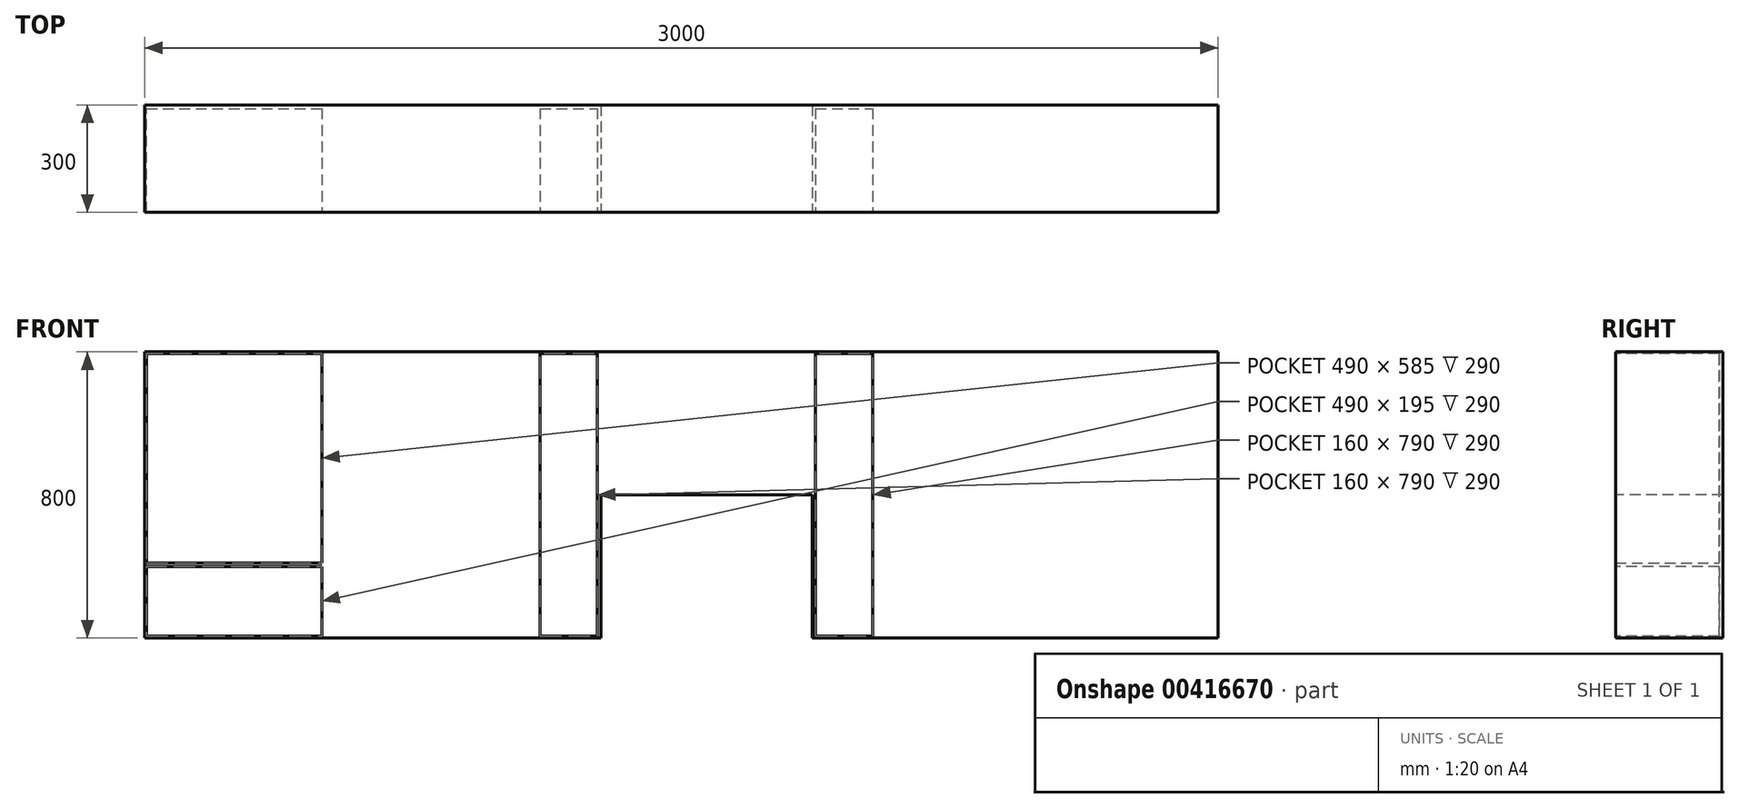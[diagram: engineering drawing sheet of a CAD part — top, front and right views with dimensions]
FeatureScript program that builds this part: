
annotation { "Feature Type Name" : "Feature", "Feature Type Description" : "" }
export const myFeature = defineFeature(function(context is Context, id is Id, definition is map)
    precondition{}
    {
        {
            var Q0;
            Q0=qCreatedBy(makeId("Front.planeOp"),FACE);
            var sketch = newSketch(context, id + "F0", { "sketchPlane" : qUnion([Q0])});
            skLineSegment(sketch, "E0.bottom", {"start": v(0, 0) * mm, "end": v(3000, 0) * mm});
            skLineSegment(sketch, "E0.top", {"start": v(0, 800) * mm, "end": v(3000, 800) * mm});
            skLineSegment(sketch, "E0.left", {"start": v(0, 0) * mm, "end": v(0, 800) * mm});
            skLineSegment(sketch, "E0.right", {"start": v(3000, 0) * mm, "end": v(3000, 800) * mm});
            skSolve(sketch);
        }
        {
            var Q0;
            Q0 = qSketchRegion(id + "F0", true);
            extrude(context, id + "F1", {"entities" : qUnion([Q0]), "depth" : 300 * mm});
        }
        {
            var Q0;
            Q0=makeQuery(id+"F1.opExtrude","CAP_FACE",FACE,{"disambiguationData":[OSD([sQuery(id+"F0.wireOp",EDGE,"E0.bottom"),sQuery(id+"F0.wireOp",EDGE,"E0.top"),sQuery(id+"F0.wireOp",EDGE,"E0.left"),sQuery(id+"F0.wireOp",EDGE,"E0.right")])],"isStart":false});
            var sketch = newSketch(context, id + "F2", { "sketchPlane" : qUnion([Q0])});
            skLineSegment(sketch, "E1.bottom", {"start": v(0, 0) * mm, "end": v(500, 0) * mm});
            skLineSegment(sketch, "E1.top", {"start": v(0, 800) * mm, "end": v(500, 800) * mm});
            skLineSegment(sketch, "E1.left", {"start": v(0, 0) * mm, "end": v(0, 800) * mm});
            skLineSegment(sketch, "E1.right", {"start": v(500, 0) * mm, "end": v(500, 800) * mm});
            skLineSegment(sketch, "E2.0", {"start": v(5, 795) * mm, "end": v(495, 795) * mm});
            skLineSegment(sketch, "E2.1", {"start": v(5, 5) * mm, "end": v(5, 795) * mm});
            skLineSegment(sketch, "E2.2", {"start": v(5, 5) * mm, "end": v(495, 5) * mm});
            skLineSegment(sketch, "E2.3", {"start": v(495, 5) * mm, "end": v(495, 795) * mm});
            skSolve(sketch);
        }
        {
            var Q0;
            Q0=makeQuery(id+"F2.imprint","IMPRINT",FACE,{"disambiguationData":[TD([[makeQuery(id+"F2.imprint","IMPRINT",EDGE,{"derivedFrom":sQuery(id+"F2.wireOp",EDGE,"E2.0")}),-1.0]])]});
            extrude(context, id + "F3", {"entities" : qUnion([Q0]), "operationType" : NewBodyOperationType.REMOVE, "oppositeDirection" : true, "depth" : 290 * mm});
        }
        {
            var Q0;
            Q0=makeQuery(id+"F1.opExtrude","CAP_FACE",FACE,{"disambiguationData":[OSD([sQuery(id+"F0.wireOp",EDGE,"E0.bottom"),sQuery(id+"F0.wireOp",EDGE,"E0.top"),sQuery(id+"F0.wireOp",EDGE,"E0.left"),sQuery(id+"F0.wireOp",EDGE,"E0.right")])],"isStart":false});
            var sketch = newSketch(context, id + "F4", { "sketchPlane" : qUnion([Q0])});
            skLineSegment(sketch, "E3.bottom", {"start": v(1100, 800) * mm, "end": v(1270, 800) * mm});
            skLineSegment(sketch, "E3.top", {"start": v(1100, 0) * mm, "end": v(1270, 0) * mm});
            skLineSegment(sketch, "E3.left", {"start": v(1100, 800) * mm, "end": v(1100, 0) * mm});
            skLineSegment(sketch, "E3.right", {"start": v(1270, 800) * mm, "end": v(1270, 0) * mm});
            skLineSegment(sketch, "E4.bottom", {"start": v(1870, 800) * mm, "end": v(2040, 800) * mm});
            skLineSegment(sketch, "E4.top", {"start": v(1870, 0) * mm, "end": v(2040, 0) * mm});
            skLineSegment(sketch, "E4.left", {"start": v(1870, 800) * mm, "end": v(1870, 0) * mm});
            skLineSegment(sketch, "E4.right", {"start": v(2040, 800) * mm, "end": v(2040, 0) * mm});
            skLineSegment(sketch, "E5.0", {"start": v(1105, 795) * mm, "end": v(1265, 795) * mm});
            skLineSegment(sketch, "E5.1", {"start": v(1105, 795) * mm, "end": v(1105, 5) * mm});
            skLineSegment(sketch, "E5.2", {"start": v(1105, 5) * mm, "end": v(1265, 5) * mm});
            skLineSegment(sketch, "E5.3", {"start": v(1265, 795) * mm, "end": v(1265, 5) * mm});
            skLineSegment(sketch, "E6.0", {"start": v(1875, 795) * mm, "end": v(2035, 795) * mm});
            skLineSegment(sketch, "E6.1", {"start": v(1875, 795) * mm, "end": v(1875, 5) * mm});
            skLineSegment(sketch, "E6.2", {"start": v(1875, 5) * mm, "end": v(2035, 5) * mm});
            skLineSegment(sketch, "E6.3", {"start": v(2035, 795) * mm, "end": v(2035, 5) * mm});
            skSolve(sketch);
        }
        {
            var Q0;
            Q0=makeQuery(id+"F4.imprint","IMPRINT",FACE,{"disambiguationData":[TD([[makeQuery(id+"F4.imprint","IMPRINT",EDGE,{"derivedFrom":sQuery(id+"F4.wireOp",EDGE,"E5.0")}),-1.0]])]});
            var Q1;
            Q1=makeQuery(id+"F4.imprint","IMPRINT",FACE,{"disambiguationData":[TD([[makeQuery(id+"F4.imprint","IMPRINT",EDGE,{"derivedFrom":sQuery(id+"F4.wireOp",EDGE,"E6.0")}),-1.0]])]});
            extrude(context, id + "F5", {"entities" : qUnion([Q0, Q1]), "operationType" : NewBodyOperationType.REMOVE, "oppositeDirection" : true, "depth" : 290 * mm});
        }
        {
            var Q0;
            Q0=makeQuery(id+"F1.opExtrude","CAP_FACE",FACE,{"disambiguationData":[OSD([sQuery(id+"F0.wireOp",EDGE,"E0.bottom"),sQuery(id+"F0.wireOp",EDGE,"E0.top"),sQuery(id+"F0.wireOp",EDGE,"E0.left"),sQuery(id+"F0.wireOp",EDGE,"E0.right")])],"isStart":false});
            var sketch = newSketch(context, id + "F6", { "sketchPlane" : qUnion([Q0])});
            skLineSegment(sketch, "E7.bottom", {"start": v(1275, 0) * mm, "end": v(1865, 0) * mm});
            skLineSegment(sketch, "E7.top", {"start": v(1275, 400) * mm, "end": v(1865, 400) * mm});
            skLineSegment(sketch, "E7.left", {"start": v(1275, 0) * mm, "end": v(1275, 400) * mm});
            skLineSegment(sketch, "E7.right", {"start": v(1865, 0) * mm, "end": v(1865, 400) * mm});
            skSolve(sketch);
        }
        {
            var Q0;
            Q0 = qSketchRegion(id + "F6", true);
            extrude(context, id + "F7", {"entities" : qUnion([Q0]), "operationType" : NewBodyOperationType.REMOVE, "endBound" : BoundingType.THROUGH_ALL, "oppositeDirection" : true, "depth" : 25 * mm});
        }
        {
            var Q0;
            Q0=makeQuery(id+"F3.boolean.opBoolean","COPY",FACE,{"derivedFrom":makeQuery(id+"F3.opExtrude","CAP_FACE",FACE,{"disambiguationData":[OSD([sQuery(id+"F2.wireOp",EDGE,"E2.0"),sQuery(id+"F2.wireOp",EDGE,"E2.1"),sQuery(id+"F2.wireOp",EDGE,"E2.2"),sQuery(id+"F2.wireOp",EDGE,"E2.3")])],"isStart":false})});
            var sketch = newSketch(context, id + "F8", { "sketchPlane" : qUnion([Q0])});
            skLineSegment(sketch, "E8", {"start": v(5, 205) * mm, "end": v(495, 205) * mm, "construction": true});
            skLineSegment(sketch, "E9.bottom", {"start": v(5, 210) * mm, "end": v(495, 210) * mm});
            skLineSegment(sketch, "E9.top", {"start": v(5, 200) * mm, "end": v(495, 200) * mm});
            skLineSegment(sketch, "E9.left", {"start": v(5, 210) * mm, "end": v(5, 200) * mm});
            skLineSegment(sketch, "E9.right", {"start": v(495, 210) * mm, "end": v(495, 200) * mm});
            skLineSegment(sketch, "E10.1.0.0", {"start": v(30, 210) * mm, "end": v(520, 210) * mm});
            skLineSegment(sketch, "E10.1.0.1", {"start": v(30, 200) * mm, "end": v(520, 200) * mm});
            skLineSegment(sketch, "E10.1.0.2", {"start": v(30, 205) * mm, "end": v(520, 205) * mm, "construction": true});
            skLineSegment(sketch, "E10.1.0.3", {"start": v(30, 210) * mm, "end": v(30, 200) * mm});
            skLineSegment(sketch, "E10.1.0.4", {"start": v(520, 210) * mm, "end": v(520, 200) * mm});
            skLineSegment(sketch, "E10.2.0.0", {"start": v(55, 210) * mm, "end": v(545, 210) * mm});
            skLineSegment(sketch, "E10.2.0.1", {"start": v(55, 200) * mm, "end": v(545, 200) * mm});
            skLineSegment(sketch, "E10.2.0.2", {"start": v(55, 205) * mm, "end": v(545, 205) * mm, "construction": true});
            skLineSegment(sketch, "E10.2.0.3", {"start": v(55, 210) * mm, "end": v(55, 200) * mm});
            skLineSegment(sketch, "E10.2.0.4", {"start": v(545, 210) * mm, "end": v(545, 200) * mm});
            skLineSegment(sketch, "E10.direction1", {"start": v(5, 200) * mm, "end": v(30, 200) * mm, "construction": true});
            skSolve(sketch);
        }
        {
            var Q0;
            Q0 = qSketchRegion(id + "F8", true);
            var Q1;
            Q1=makeQuery(id+"F1.opExtrude","CAP_FACE",FACE,{"disambiguationData":[OSD([sQuery(id+"F0.wireOp",EDGE,"E0.bottom"),sQuery(id+"F0.wireOp",EDGE,"E0.top"),sQuery(id+"F0.wireOp",EDGE,"E0.left"),sQuery(id+"F0.wireOp",EDGE,"E0.right")])],"isStart":false});
            extrude(context, id + "F9", {"entities" : qUnion([Q0]), "operationType" : NewBodyOperationType.ADD, "endBound" : BoundingType.UP_TO_SURFACE, "endBoundEntityFace" : qUnion([Q1]), "depth" : 25 * mm});
        }
    });
